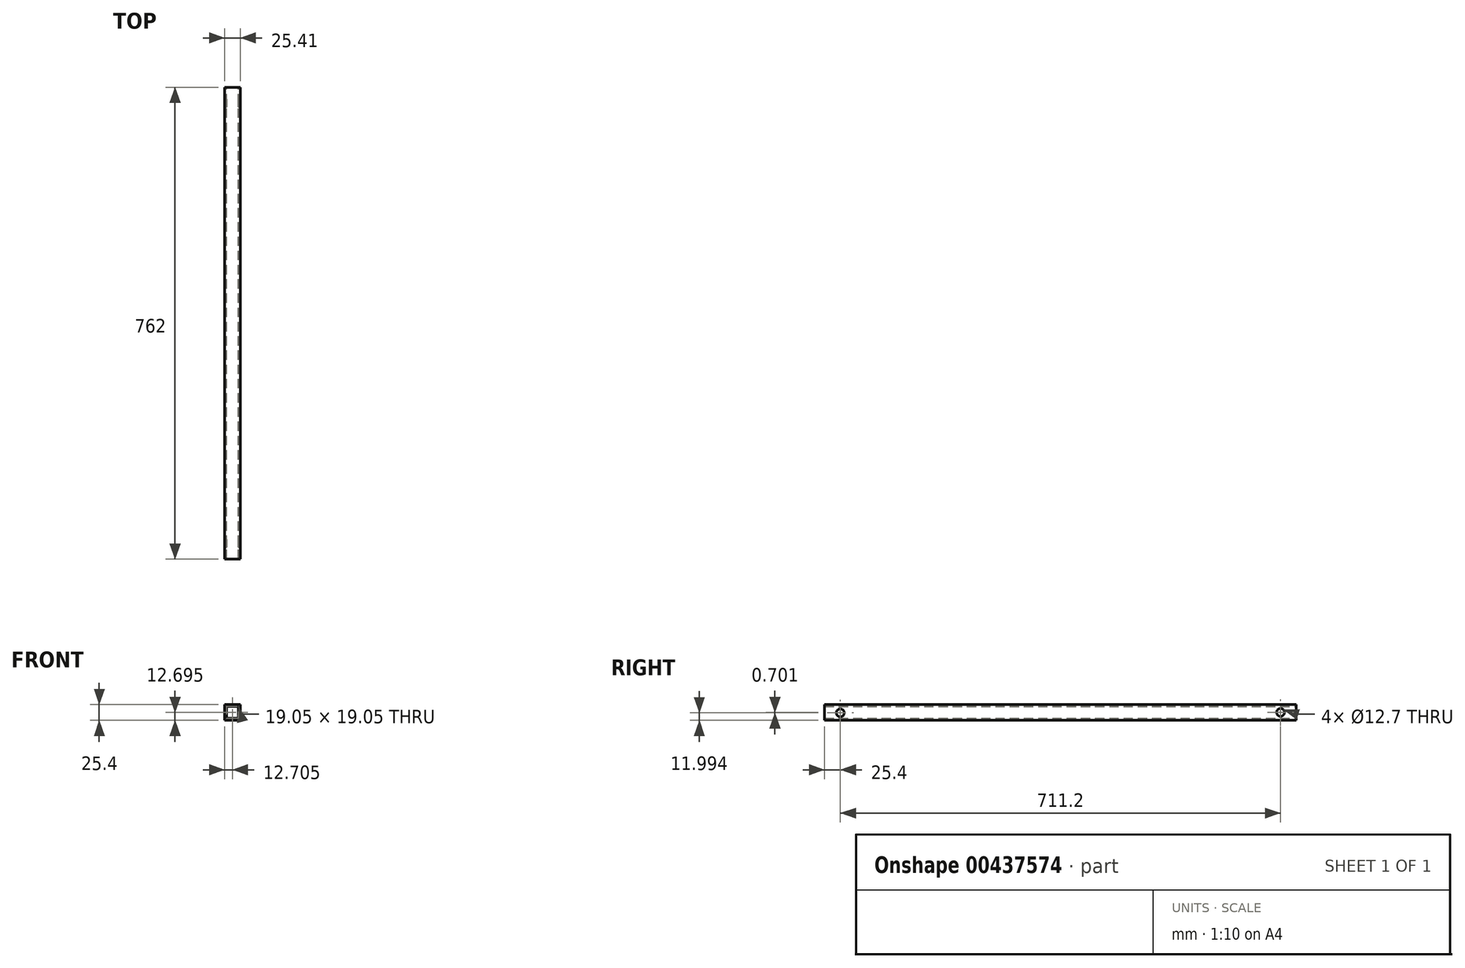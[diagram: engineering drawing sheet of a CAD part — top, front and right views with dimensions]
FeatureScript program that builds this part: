
annotation { "Feature Type Name" : "Feature", "Feature Type Description" : "" }
export const myFeature = defineFeature(function(context is Context, id is Id, definition is map)
    precondition{}
    {
        {
            var Q0;
            Q0=qCreatedBy(makeId("Front.planeOp"),FACE);
            var sketch = newSketch(context, id + "F0", { "sketchPlane" : qUnion([Q0])});
            skLineSegment(sketch, "E0.bottom", {"start": v(-22.23, 22.23) * mm, "end": v(3.17, 22.23) * mm});
            skLineSegment(sketch, "E0.top", {"start": v(-22.23, -3.18) * mm, "end": v(3.18, -3.18) * mm});
            skLineSegment(sketch, "E0.left", {"start": v(-22.23, 22.23) * mm, "end": v(-22.23, -3.18) * mm});
            skLineSegment(sketch, "E0.right", {"start": v(3.17, 22.23) * mm, "end": v(3.18, -3.18) * mm});
            skLineSegment(sketch, "E1.bottom", {"start": v(-19.05, 19.05) * mm, "end": v(0, 19.05) * mm});
            skLineSegment(sketch, "E1.top", {"start": v(-19.05, 0) * mm, "end": v(0, 0) * mm});
            skLineSegment(sketch, "E1.left", {"start": v(-19.05, 19.05) * mm, "end": v(-19.05, 0) * mm});
            skLineSegment(sketch, "E1.right", {"start": v(0, 19.05) * mm, "end": v(0, 0) * mm});
            skSolve(sketch);
        }
        {
            var Q0;
            Q0=qSketchRegion(id+"F0",true);
            extrude(context, id + "F1", {"entities" : qUnion([Q0]), "depth" : 762 * mm});
        }
        {
            var Q0;
            Q0=makeQuery(id+"F1.opExtrude","SWEPT_FACE",FACE,{"disambiguationData":[OSD([sQuery(id+"F0.wireOp",EDGE,"E0.right")])]});
            var sketch = newSketch(context, id + "F2", { "sketchPlane" : qUnion([Q0])});
            skPoint(sketch, "E2", {"position": v(-736.6, 8.82) * mm});
            skSolve(sketch);
        }
        {
            var Q0;
            Q0=sQuery(id+"F2.wireOp",VERTEX,"E2");
            var Q1;
            Q1=makeQuery(id+"F1.opExtrude","SWEPT_BODY",BODY,{"disambiguationData":[OSD([sQuery(id+"F0.wireOp",EDGE,"E0.bottom"),sQuery(id+"F0.wireOp",EDGE,"E0.top"),sQuery(id+"F0.wireOp",EDGE,"E0.left"),sQuery(id+"F0.wireOp",EDGE,"E0.right"),sQuery(id+"F0.wireOp",EDGE,"E1.bottom"),sQuery(id+"F0.wireOp",EDGE,"E1.top"),sQuery(id+"F0.wireOp",EDGE,"E1.left"),sQuery(id+"F0.wireOp",EDGE,"E1.right")])]});
            hole(context, id + "F3", {"style" : HoleStyle.SIMPLE, "endStyle" : HoleEndStyle.THROUGH, "holeDiameter" : 12.7 * mm, "isTappedThrough" : true, "tappedDepth" : 12.7 * mm, "tapClearance" : 3, "locations" : qUnion([Q0]), "scope" : qUnion([Q1])});
        }
        {
            var Q0;
            Q0=makeQuery(id+"F1.opExtrude","SWEPT_FACE",FACE,{"disambiguationData":[OSD([sQuery(id+"F0.wireOp",EDGE,"E0.right")])]});
            var sketch = newSketch(context, id + "F4", { "sketchPlane" : qUnion([Q0])});
            skPoint(sketch, "E3", {"position": v(-25.4, 9.52) * mm});
            skSolve(sketch);
        }
        {
            var Q0;
            Q0=sQuery(id+"F4.wireOp",VERTEX,"E3");
            var Q1;
            Q1=makeQuery(id+"F1.opExtrude","SWEPT_BODY",BODY,{"disambiguationData":[OSD([sQuery(id+"F0.wireOp",EDGE,"E0.bottom"),sQuery(id+"F0.wireOp",EDGE,"E0.top"),sQuery(id+"F0.wireOp",EDGE,"E0.left"),sQuery(id+"F0.wireOp",EDGE,"E0.right"),sQuery(id+"F0.wireOp",EDGE,"E1.bottom"),sQuery(id+"F0.wireOp",EDGE,"E1.top"),sQuery(id+"F0.wireOp",EDGE,"E1.left"),sQuery(id+"F0.wireOp",EDGE,"E1.right")])]});
            hole(context, id + "F5", {"style" : HoleStyle.SIMPLE, "endStyle" : HoleEndStyle.THROUGH, "holeDiameter" : 12.7 * mm, "isTappedThrough" : true, "tappedDepth" : 12.7 * mm, "tapClearance" : 3, "locations" : qUnion([Q0]), "scope" : qUnion([Q1])});
        }
    });
